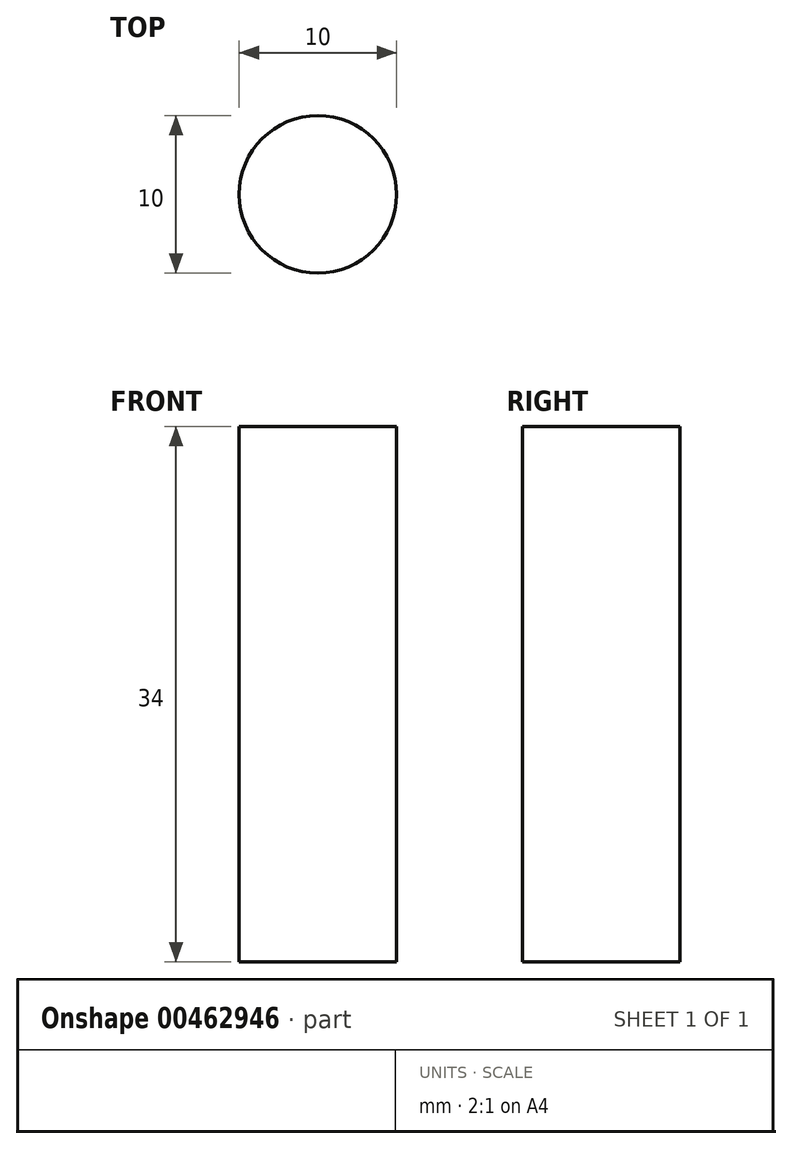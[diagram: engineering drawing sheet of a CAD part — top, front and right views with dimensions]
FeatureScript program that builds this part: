
annotation { "Feature Type Name" : "Feature", "Feature Type Description" : "" }
export const myFeature = defineFeature(function(context is Context, id is Id, definition is map)
    precondition{}
    {
        {
            var Q0;
            Q0=qCreatedBy(makeId("Top.planeOp"),FACE);
            var sketch = newSketch(context, id + "F0", { "sketchPlane" : qUnion([Q0])});
            skCircle(sketch, "E0", {"center": v(0, 0) * mm, "radius": 5 * mm});
            skSolve(sketch);
        }
        {
            var Q0;
            Q0 = qSketchRegion(id + "F0", true);
            extrude(context, id + "F1", {"entities" : qUnion([Q0]), "depth" : 34 * mm});
        }
    });
